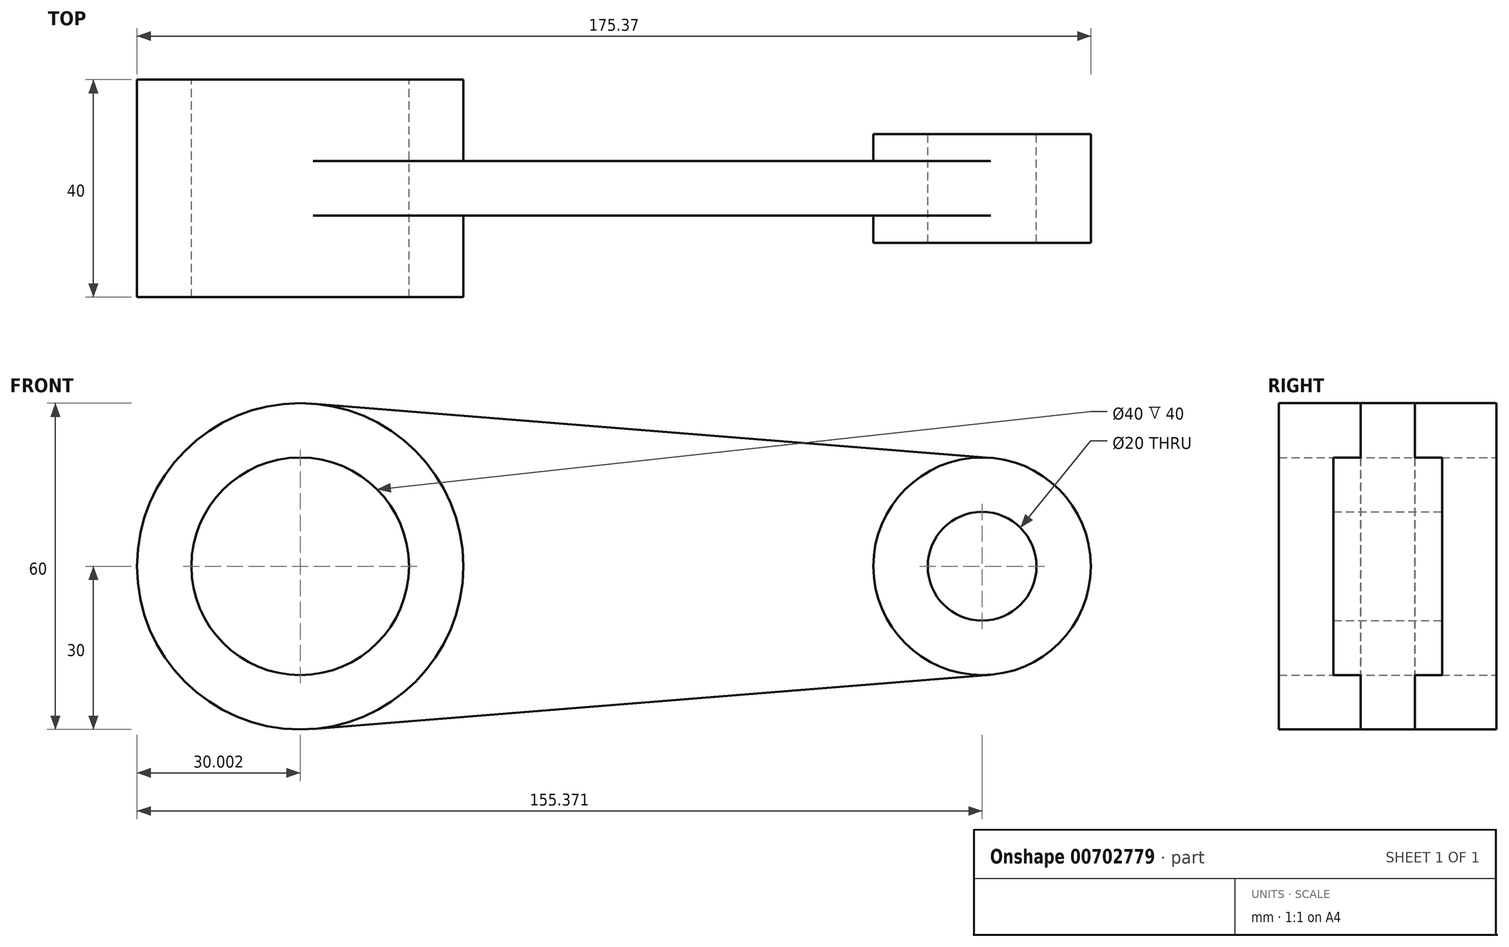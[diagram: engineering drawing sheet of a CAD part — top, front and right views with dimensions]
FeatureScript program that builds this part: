
annotation { "Feature Type Name" : "Feature", "Feature Type Description" : "" }
export const myFeature = defineFeature(function(context is Context, id is Id, definition is map)
    precondition{}
    {
        {
            var Q0;
            Q0=qCreatedBy(makeId("Front.planeOp"),FACE);
            var sketch = newSketch(context, id + "F0", { "sketchPlane" : qUnion([Q0])});
            skCircle(sketch, "E0", {"center": v(-79.66, 0) * mm, "radius": 30 * mm});
            skCircle(sketch, "E1", {"center": v(-79.66, 0) * mm, "radius": 20 * mm});
            skCircle(sketch, "E2", {"center": v(45.71, 0) * mm, "radius": 20 * mm});
            skCircle(sketch, "E3", {"center": v(45.71, 0) * mm, "radius": 10 * mm});
            skLineSegment(sketch, "E4", {"start": v(-77.26, 29.9) * mm, "end": v(47.3, 19.94) * mm});
            skLineSegment(sketch, "E5", {"start": v(-77.26, -29.9) * mm, "end": v(47.3, -19.94) * mm});
            skSolve(sketch);
        }
        {
            var Q0;
            {var subQ0=sQuery(id+"F0.wireOp",EDGE,"E4");Q0=makeQuery(id+"F0.imprint","IMPRINT",FACE,{"disambiguationData":[TD([[makeQuery(id+"F0.imprint","IMPRINT",EDGE,{"derivedFrom":subQ0}),-1.0]])]});}
            extrude(context, id + "F1", {"entities" : qUnion([Q0]), "depth" : 10 * mm, "offsetDistance" : 25 * mm});
        }
        {
            var Q0;
            Q0=makeQuery(id+"F0.imprint","IMPRINT",FACE,{"disambiguationData":[TD([[makeQuery(id+"F0.imprint","IMPRINT",EDGE,{"derivedFrom":sQuery(id+"F0.wireOp",EDGE,"E1")}),-1.0]])]});
            extrude(context, id + "F2", {"entities" : qUnion([Q0]), "operationType" : NewBodyOperationType.ADD, "depth" : 25 * mm, "offsetDistance" : 25 * mm});
        }
        {
            var Q0;
            Q0=makeQuery(id+"F0.imprint","IMPRINT",FACE,{"disambiguationData":[TD([[makeQuery(id+"F0.imprint","IMPRINT",EDGE,{"derivedFrom":sQuery(id+"F0.wireOp",EDGE,"E1")}),-1.0]])]});
            extrude(context, id + "F3", {"entities" : qUnion([Q0]), "operationType" : NewBodyOperationType.ADD, "oppositeDirection" : true, "depth" : 15 * mm, "offsetDistance" : 25 * mm});
        }
        {
            var Q0;
            Q0=makeQuery(id+"F0.imprint","IMPRINT",FACE,{"disambiguationData":[TD([[makeQuery(id+"F0.imprint","IMPRINT",EDGE,{"derivedFrom":sQuery(id+"F0.wireOp",EDGE,"E3")}),-1.0]])]});
            extrude(context, id + "F4", {"entities" : qUnion([Q0]), "operationType" : NewBodyOperationType.ADD, "depth" : 15 * mm, "offsetDistance" : 25 * mm});
        }
        {
            var Q0;
            Q0=makeQuery(id+"F0.imprint","IMPRINT",FACE,{"disambiguationData":[TD([[makeQuery(id+"F0.imprint","IMPRINT",EDGE,{"derivedFrom":sQuery(id+"F0.wireOp",EDGE,"E3")}),-1.0]])]});
            extrude(context, id + "F5", {"entities" : qUnion([Q0]), "operationType" : NewBodyOperationType.ADD, "oppositeDirection" : true, "depth" : 5 * mm, "offsetDistance" : 25 * mm});
        }
    });
